# Revit family: Sensor-Lutron-Partition-GRX
name_source: partatom
category: Lighting Devices
revit_build: Autodesk Revit 2017 (Build: 20160720_1515(x64)
units: mm (PartAtom-declared; Revit-internal decimal feet)

## family parameters
Cut with Voids When Loaded = No
Host = Face
Maintain Annotation Orientation = No
OmniClass Number = 23.85.80.11.27
OmniClass Title = Lighting Controls
Part Type = Normal
Room Calculation Point = No
Round Connector Dimension = Use Diameter
Shared = No

## types (2) — shared parameters
Assembly Code = D5030800
Default Elevation = 0' - 0"
Instruction Sheet Link = http://www.lutron.com
Label = PS
Manufacturer = Lutron Electronics Co., Inc
Manufacturer Fax Number = 610-282-1243
Material = Plastic - Lutron - White
Model = GRX-IRPS-WH
Overall Depth = 0' - 1 1/2"
Overall Height = 0' - 4 11/16"
Overall Width = 0' - 2 15/16"
Performance URL = http://www.lutron.com
Product Documentation Link = http://www.lutron.com
Product Page URL = http://www.lutron.com
Series = GRAFIK Eye
URL = http://www.lutron.com
Version = 2017 - v1.0b
Video Link = https://www.youtube.com
Warranty URL = http://www.lutron.com
zero-valued in all types: Cost

## per-type parameters (varying)
| type | Description | Product Name |
| GRX-IRPS-WH TX | Transmitter Partition Sensor | Transmitter Partition Sensor |
| GRX-IRPS-WH RX | Receiver Partition Sensor | Receiver Partition Sensor |

## geometry (parser evidence)
native form markers: Blend x4, Sweep x3
no freeform markers — native parametric forms only
